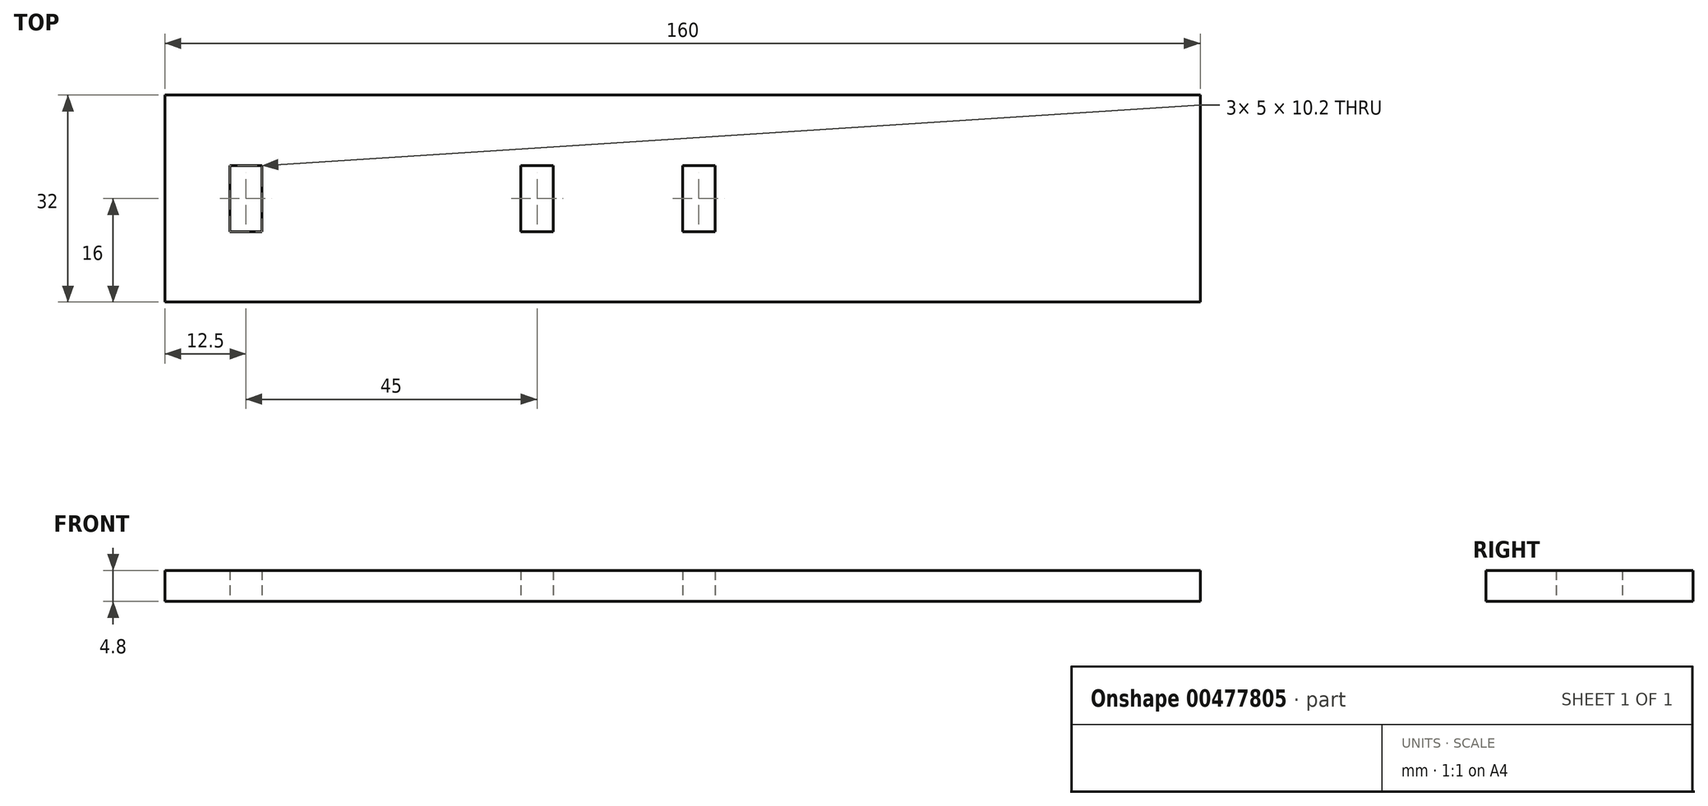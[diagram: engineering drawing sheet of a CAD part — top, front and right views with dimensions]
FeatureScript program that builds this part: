
annotation { "Feature Type Name" : "Feature", "Feature Type Description" : "" }
export const myFeature = defineFeature(function(context is Context, id is Id, definition is map)
    precondition{}
    {
        {
            var Q0;
            Q0=qCreatedBy(makeId("Top.planeOp"),FACE);
            var sketch = newSketch(context, id + "F0", { "sketchPlane" : qUnion([Q0])});
            skLineSegment(sketch, "E0.bottom", {"start": v(0, 0) * mm, "end": v(160, 0) * mm});
            skLineSegment(sketch, "E0.top", {"start": v(0, 32) * mm, "end": v(160, 32) * mm});
            skLineSegment(sketch, "E0.left", {"start": v(0, 0) * mm, "end": v(0, 32) * mm});
            skLineSegment(sketch, "E0.right", {"start": v(160, 0) * mm, "end": v(160, 32) * mm});
            skLineSegment(sketch, "E1.bottom", {"start": v(55, 21.1) * mm, "end": v(60, 21.1) * mm});
            skLineSegment(sketch, "E1.top", {"start": v(55, 10.9) * mm, "end": v(60, 10.9) * mm});
            skLineSegment(sketch, "E1.left", {"start": v(55, 21.1) * mm, "end": v(55, 10.9) * mm});
            skLineSegment(sketch, "E1.right", {"start": v(60, 21.1) * mm, "end": v(60, 10.9) * mm});
            skLineSegment(sketch, "E2.bottom", {"start": v(10, 21.1) * mm, "end": v(15, 21.1) * mm});
            skLineSegment(sketch, "E2.top", {"start": v(10, 10.9) * mm, "end": v(15, 10.9) * mm});
            skLineSegment(sketch, "E2.left", {"start": v(10, 21.1) * mm, "end": v(10, 10.9) * mm});
            skLineSegment(sketch, "E2.right", {"start": v(15, 21.1) * mm, "end": v(15, 10.9) * mm});
            skLineSegment(sketch, "E3.bottom", {"start": v(80, 21.1) * mm, "end": v(85, 21.1) * mm});
            skLineSegment(sketch, "E3.top", {"start": v(80, 10.9) * mm, "end": v(85, 10.9) * mm});
            skLineSegment(sketch, "E3.left", {"start": v(80, 21.1) * mm, "end": v(80, 10.9) * mm});
            skLineSegment(sketch, "E3.right", {"start": v(85, 21.1) * mm, "end": v(85, 10.9) * mm});
            skSolve(sketch);
        }
        {
            var Q0;
            Q0=makeQuery(id+"F0.imprint","IMPRINT",FACE,{"disambiguationData":[TD([[makeQuery(id+"F0.imprint","IMPRINT",EDGE,{"derivedFrom":sQuery(id+"F0.wireOp",EDGE,"E0.bottom")}),1.0]])]});
            extrude(context, id + "F1", {"entities" : qUnion([Q0]), "depth" : 4.8 * mm});
        }
    });
